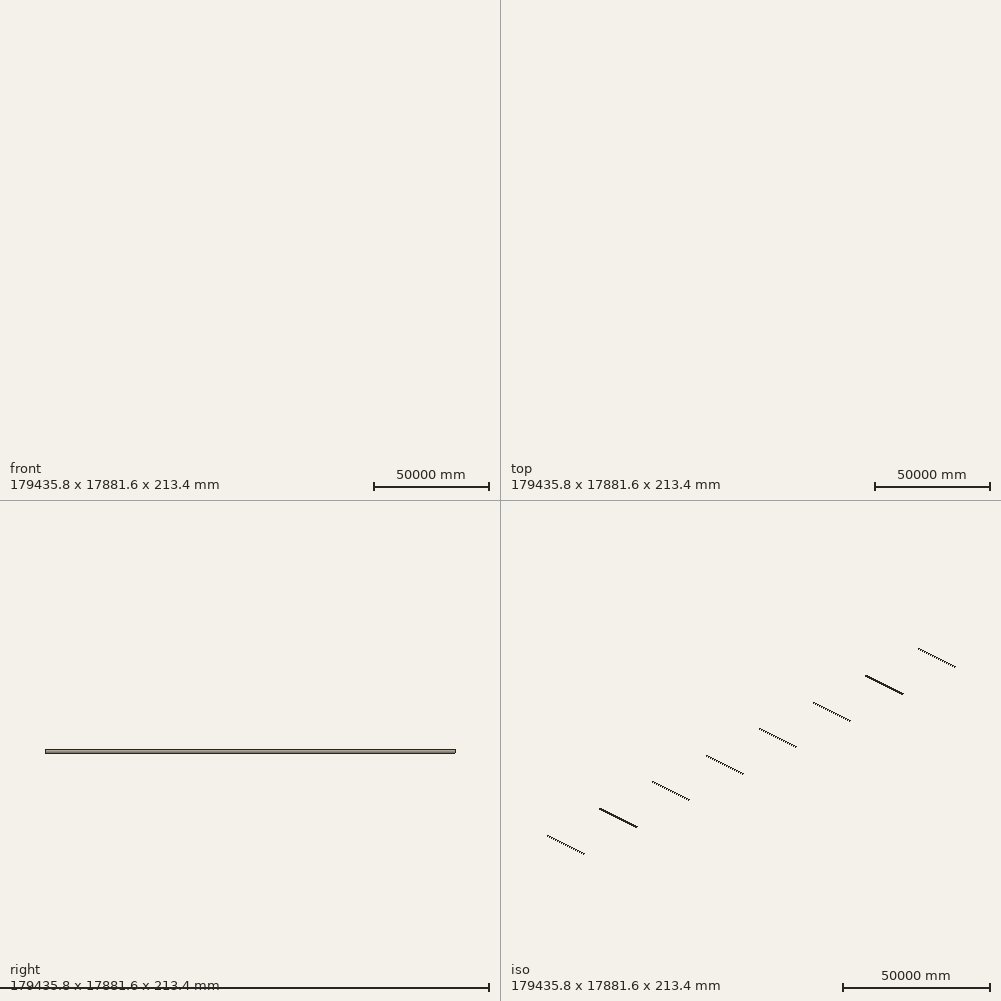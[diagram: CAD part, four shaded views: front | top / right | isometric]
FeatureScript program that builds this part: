
annotation { "Feature Type Name" : "Feature", "Feature Type Description" : "" }
export const myFeature = defineFeature(function(context is Context, id is Id, definition is map)
    precondition{}
    {
        {
            var Q0;
            Q0=qCreatedBy(makeId("Top.planeOp"),FACE);
            cPlane(context, id + "F0", {"entities" : qUnion([Q0]), "cplaneType" : CPlaneType.OFFSET, "offset" : 627.38 * mm, "oppositeDirection" : true, "width" : 152.4 * mm, "height" : 152.4 * mm});
        }
        {
            var Q0;
            Q0=qCreatedBy(makeId("Front.planeOp"),FACE);
            var sketch = newSketch(context, id + "F1", { "sketchPlane" : qUnion([Q0])});
            skCircle(sketch, "E0", {"center": v(12014.2, -525.78) * mm, "radius": 106.68 * mm});
            skCircle(sketch, "E1", {"center": v(12014.2, -525.78) * mm, "radius": 101.6 * mm});
            skLineSegment(sketch, "E2", {"start": v(0, 0) * mm, "end": v(13897.16, 0) * mm, "construction": true});
            skCircle(sketch, "E3.1.0.0", {"center": v(37617.4, -525.78) * mm, "radius": 101.6 * mm});
            skCircle(sketch, "E3.1.0.1", {"center": v(37617.4, -525.78) * mm, "radius": 106.68 * mm});
            skCircle(sketch, "E3.2.0.0", {"center": v(63220.6, -525.78) * mm, "radius": 101.6 * mm});
            skCircle(sketch, "E3.2.0.1", {"center": v(63220.6, -525.78) * mm, "radius": 106.68 * mm});
            skCircle(sketch, "E3.3.0.0", {"center": v(88823.8, -525.78) * mm, "radius": 101.6 * mm});
            skCircle(sketch, "E3.3.0.1", {"center": v(88823.8, -525.78) * mm, "radius": 106.68 * mm});
            skCircle(sketch, "E3.4.0.0", {"center": v(114427, -525.78) * mm, "radius": 101.6 * mm});
            skCircle(sketch, "E3.4.0.1", {"center": v(114427, -525.78) * mm, "radius": 106.68 * mm});
            skCircle(sketch, "E3.5.0.0", {"center": v(140030.2, -525.78) * mm, "radius": 101.6 * mm});
            skCircle(sketch, "E3.5.0.1", {"center": v(140030.2, -525.78) * mm, "radius": 106.68 * mm});
            skCircle(sketch, "E3.6.0.0", {"center": v(165633.4, -525.78) * mm, "radius": 101.6 * mm});
            skCircle(sketch, "E3.6.0.1", {"center": v(165633.4, -525.78) * mm, "radius": 106.68 * mm});
            skCircle(sketch, "E3.7.0.0", {"center": v(191236.6, -525.78) * mm, "radius": 101.6 * mm});
            skCircle(sketch, "E3.7.0.1", {"center": v(191236.6, -525.78) * mm, "radius": 106.68 * mm});
            skLineSegment(sketch, "E3.direction1", {"start": v(12014.2, -525.78) * mm, "end": v(37617.4, -525.78) * mm, "construction": true});
            skSolve(sketch);
        }
        {
            var Q0;
            Q0 = qSketchRegion(id + "F1", true);
            extrude(context, id + "F2", {"entities" : qUnion([Q0]), "oppositeDirection" : true, "depth" : 17068.8 * mm, "hasSecondDirection" : true, "secondDirectionOppositeDirection" : false, "secondDirectionDepth" : 812.8 * mm});
        }
    });
